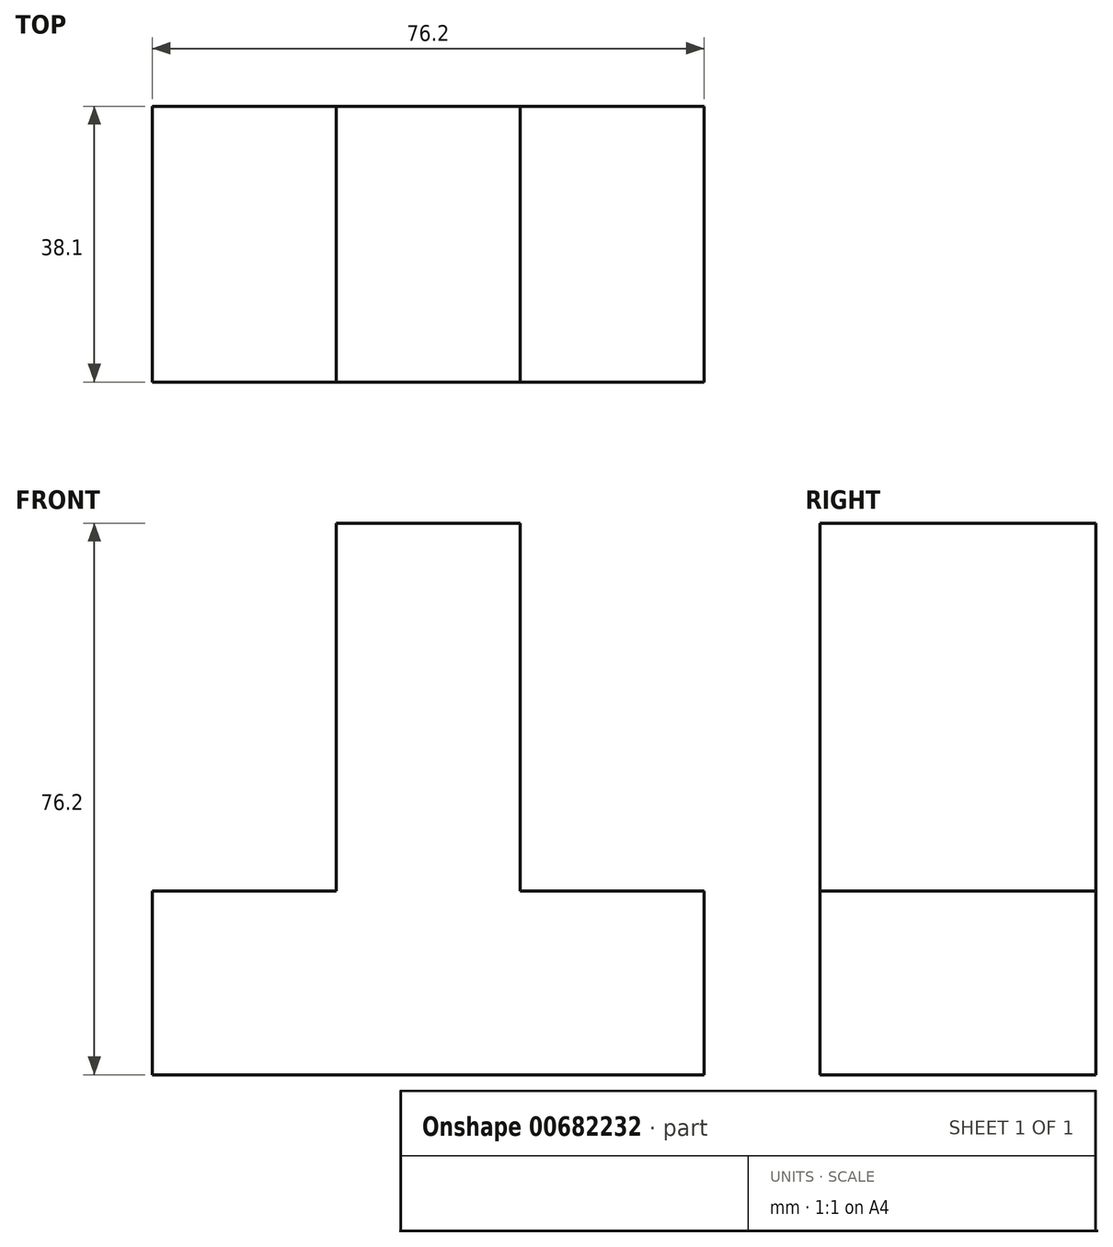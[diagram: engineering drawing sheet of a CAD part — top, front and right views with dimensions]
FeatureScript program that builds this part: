
annotation { "Feature Type Name" : "Feature", "Feature Type Description" : "" }
export const myFeature = defineFeature(function(context is Context, id is Id, definition is map)
    precondition{}
    {
        {
            var Q0;
            Q0=qCreatedBy(makeId("Front.planeOp"),FACE);
            var sketch = newSketch(context, id + "F0", { "sketchPlane" : qUnion([Q0])});
            skLineSegment(sketch, "E0", {"start": v(-24.05, -43.07) * mm, "end": v(52.15, -43.07) * mm});
            skLineSegment(sketch, "E1", {"start": v(-24.05, -43.07) * mm, "end": v(-24.05, -17.67) * mm});
            skLineSegment(sketch, "E2", {"start": v(-24.05, -17.67) * mm, "end": v(1.35, -17.67) * mm});
            skLineSegment(sketch, "E3", {"start": v(1.35, -17.67) * mm, "end": v(1.35, 33.13) * mm});
            skLineSegment(sketch, "E4", {"start": v(1.35, 33.13) * mm, "end": v(26.75, 33.13) * mm});
            skLineSegment(sketch, "E5", {"start": v(26.75, 33.13) * mm, "end": v(26.75, -17.67) * mm});
            skLineSegment(sketch, "E6", {"start": v(26.75, -17.67) * mm, "end": v(52.15, -17.67) * mm});
            skLineSegment(sketch, "E7", {"start": v(52.15, -17.67) * mm, "end": v(52.15, -43.07) * mm});
            skSolve(sketch);
        }
        {
            var Q0;
            Q0=makeQuery(id+"F0.imprint","IMPRINT",FACE,{"disambiguationData":[TD([[makeQuery(id+"F0.imprint","IMPRINT",EDGE,{"derivedFrom":sQuery(id+"F0.wireOp",EDGE,"E0")}),1.0]])]});
            extrude(context, id + "F1", {"entities" : qUnion([Q0]), "depth" : 38.1 * mm, "offsetDistance" : 25.4 * mm});
        }
    });
